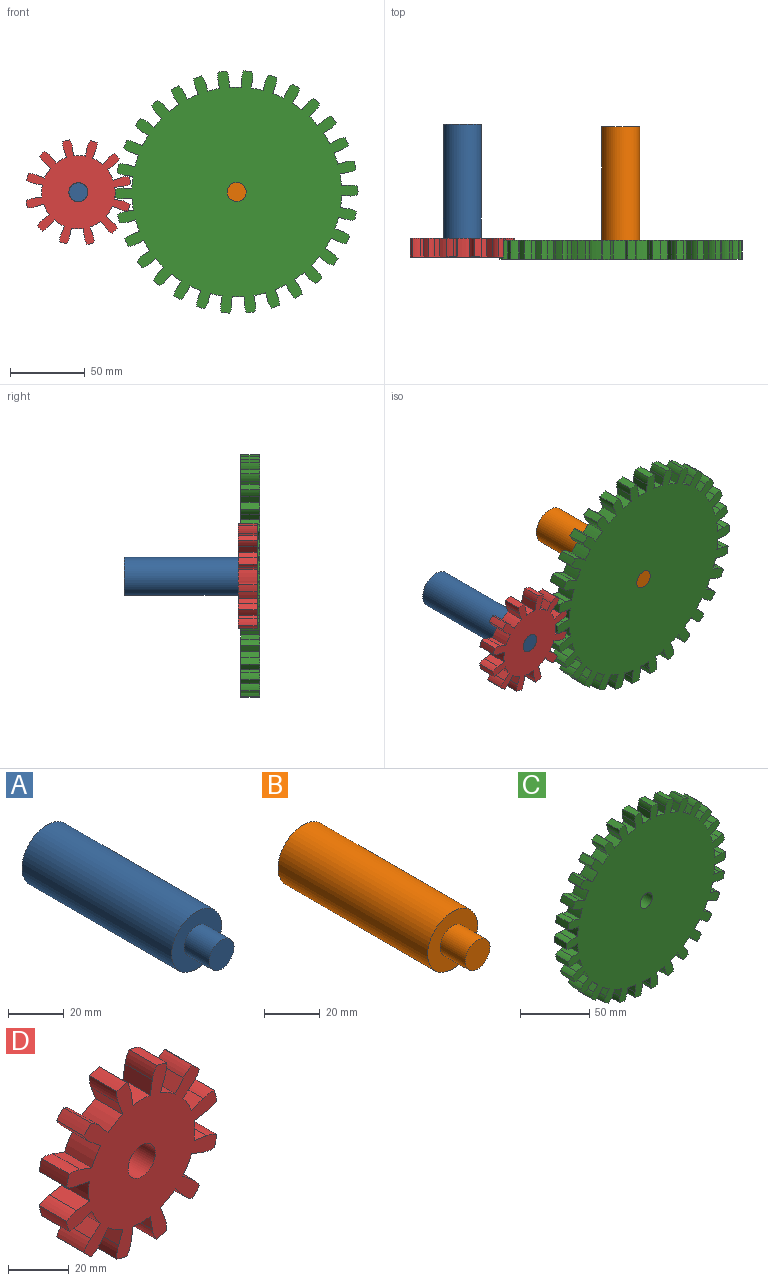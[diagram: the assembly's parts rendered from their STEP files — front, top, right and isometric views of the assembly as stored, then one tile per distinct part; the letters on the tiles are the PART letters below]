
ASSEMBLY  parts=4 mates=2
PART A: 5 faces, bbox 25.4x88.9x25.4 mm
  f0: plane 25.4x25.4mm, normal (0,-1,0), area 380mm2, adj f1,f3
  f1: cylinder r=12.7mm len=76.2mm, axis (0,-1,0), area 6080.5mm2, adj f0,f2
  f2: plane 25.4x25.4mm, normal (0,1,0), area 506.7mm2, adj f1
  f3: cylinder r=6.35mm len=12.7mm, axis (0,1,0), area 506.7mm2, adj f0,f4
  f4: plane 12.7x12.7mm, normal (0,-1,0), area 126.7mm2, adj f3
PART B: 5 faces, bbox 25.4x88.9x25.4 mm
  f0: plane 25.4x25.4mm, normal (0,-1,0), area 380mm2, adj f1,f3
  f1: cylinder r=12.7mm len=76.2mm, axis (0,-1,0), area 6080.5mm2, adj f0,f2
  f2: plane 25.4x25.4mm, normal (0,1,0), area 506.7mm2, adj f1
  f3: cylinder r=6.35mm len=12.7mm, axis (0,1,0), area 506.7mm2, adj f0,f4
  f4: plane 12.7x12.7mm, normal (0,-1,0), area 126.7mm2, adj f3
PART C: 183 faces, bbox 162.6x12.7x162.2 mm
  f0: plane 162.56x162.15mm, normal (0,-1,0), area 17686.6mm2, adj f2,f3,f4,f5,f6,f7,f8,f9
  f1: plane 162.56x162.15mm, normal (0,1,0), area 17686.6mm2, adj f2,f3,f4,f5,f6,f7,f8,f9
  f2: cylinder r=81.28mm len=12.7mm, axis (0,-1,0), area 70.3mm2, adj f0,f1,f177,f181
  f3: cylinder r=81.28mm len=12.7mm, axis (0,-1,0), area 70.3mm2, adj f0,f1,f172,f176
  f4: cylinder r=81.28mm len=12.7mm, axis (0,-1,0), area 70.3mm2, adj f0,f1,f167,f171
  f5: cylinder r=81.28mm len=12.7mm, axis (0,-1,0), area 70.3mm2, adj f0,f1,f162,f166
  f6: cylinder r=81.28mm len=12.7mm, axis (0,-1,0), area 70.3mm2, adj f0,f1,f157,f161
  f7: cylinder r=81.28mm len=12.7mm, axis (0,-1,0), area 70.3mm2, adj f0,f1,f152,f156
  f8: cylinder r=81.28mm len=12.7mm, axis (0,-1,0), area 70.3mm2, adj f0,f1,f147,f151
  f9: cylinder r=81.28mm len=12.7mm, axis (0,-1,0), area 70.3mm2, adj f0,f1,f142,f146
  f10: cylinder r=81.28mm len=12.7mm, axis (0,-1,0), area 70.3mm2, adj f0,f1,f137,f141
  f11: cylinder r=81.28mm len=12.7mm, axis (0,-1,0), area 70.3mm2, adj f0,f1,f132,f136
  f12: cylinder r=81.28mm len=12.7mm, axis (0,-1,0), area 70.3mm2, adj f0,f1,f127,f131
  f13: cylinder r=81.28mm len=12.7mm, axis (0,-1,0), area 70.3mm2, adj f0,f1,f122,f126
  f14: cylinder r=81.28mm len=12.7mm, axis (0,-1,0), area 70.3mm2, adj f0,f1,f117,f121
  f15: cylinder r=81.28mm len=12.7mm, axis (0,-1,0), area 70.3mm2, adj f0,f1,f112,f116
  f16: cylinder r=81.28mm len=12.7mm, axis (0,-1,0), area 70.3mm2, adj f0,f1,f107,f111
  f17: cylinder r=81.28mm len=12.7mm, axis (0,-1,0), area 70.3mm2, adj f0,f1,f102,f106
  f18: cylinder r=81.28mm len=12.7mm, axis (0,-1,0), area 70.3mm2, adj f0,f1,f97,f101
  f19: cylinder r=81.28mm len=12.7mm, axis (0,-1,0), area 70.3mm2, adj f0,f1,f92,f96
  f20: cylinder r=81.28mm len=12.7mm, axis (0,-1,0), area 70.3mm2, adj f0,f1,f87,f91
  f21: cylinder r=81.28mm len=12.7mm, axis (0,-1,0), area 70.3mm2, adj f0,f1,f82,f86
  f22: cylinder r=81.28mm len=12.7mm, axis (0,-1,0), area 70.3mm2, adj f0,f1,f77,f81
  f23: cylinder r=81.28mm len=12.7mm, axis (0,-1,0), area 70.3mm2, adj f0,f1,f72,f76
  f24: cylinder r=81.28mm len=12.7mm, axis (0,-1,0), area 70.3mm2, adj f0,f1,f67,f71
  f25: cylinder r=81.28mm len=12.7mm, axis (0,-1,0), area 70.3mm2, adj f0,f1,f62,f66
  f26: cylinder r=81.28mm len=12.7mm, axis (0,-1,0), area 70.3mm2, adj f0,f1,f57,f61
  f27: cylinder r=81.28mm len=12.7mm, axis (0,-1,0), area 70.3mm2, adj f0,f1,f52,f56
  f28: cylinder r=81.28mm len=12.7mm, axis (0,-1,0), area 70.3mm2, adj f0,f1,f47,f51
  f29: cylinder r=81.28mm len=12.7mm, axis (0,-1,0), area 70.3mm2, adj f0,f1,f41,f46
  f30: cylinder r=81.28mm len=12.7mm, axis (0,-1,0), area 70.3mm2, adj f0,f1,f36,f40
  f31: cylinder r=81.28mm len=12.7mm, axis (0,-1,0), area 70.3mm2, adj f0,f1,f35,f182
  f32: cylinder r=6.35mm len=12.7mm, axis (0,-1,0), area 506.7mm2, adj f0,f1
  f33: cylinder r=70.32mm len=12.7mm, axis (0,1,0), area 101.4mm2, adj f0,f1,f34,f37
  f34: plane 12.7x5.87mm, normal (-1,0,0.06), area 74.6mm2, adj f0,f1,f33,f35
  f35: cylinder r=11.96mm len=12.7mm, axis (0,1,0), area 66.5mm2, adj f0,f1,f31,f34
  f36: cylinder r=11.96mm len=12.7mm, axis (0,1,0), area 66.5mm2, adj f0,f1,f30,f37
  f37: plane 12.7x5.87mm, normal (1,0,0.06), area 74.6mm2, adj f0,f1,f33,f36
  f38: cylinder r=70.32mm len=12.7mm, axis (0,1,0), area 101.4mm2, adj f0,f1,f39,f42
  f39: plane 12.7x5.81mm, normal (-0.99,0,-0.15), area 74.6mm2, adj f0,f1,f38,f40
  f40: cylinder r=11.96mm len=12.7mm, axis (0,1,0), area 66.5mm2, adj f0,f1,f30,f39
  f41: cylinder r=11.96mm len=12.7mm, axis (0,1,0), area 66.5mm2, adj f0,f1,f29,f42
  f42: plane 12.7x5.67mm, normal (0.96,0,0.26), area 74.6mm2, adj f0,f1,f38,f41
  f43: cylinder r=70.32mm len=12.7mm, axis (0,1,0), area 101.4mm2, adj f0,f1,f44,f45
  f44: plane 12.7x5.5mm, normal (-0.94,0,-0.35), area 74.6mm2, adj f0,f1,f43,f46
  f45: plane 12.7x5.23mm, normal (0.89,0,0.46), area 74.6mm2, adj f0,f1,f43,f47
  f46: cylinder r=11.96mm len=12.7mm, axis (0,1,0), area 66.5mm2, adj f0,f1,f29,f44
  f47: cylinder r=11.96mm len=12.7mm, axis (0,1,0), area 66.5mm2, adj f0,f1,f28,f45
  f48: cylinder r=70.32mm len=12.7mm, axis (0,1,0), area 101.4mm2, adj f0,f1,f49,f50
  f49: plane 12.7x4.94mm, normal (-0.84,0,-0.54), area 74.6mm2, adj f0,f1,f48,f51
  f50: plane 12.7x4.55mm, normal (0.77,0,0.63), area 74.6mm2, adj f0,f1,f48,f52
  f51: cylinder r=11.96mm len=12.7mm, axis (0,1,0), area 66.5mm2, adj f0,f1,f28,f49
  f52: cylinder r=11.96mm len=12.7mm, axis (0,1,0), area 66.5mm2, adj f0,f1,f27,f50
  f53: cylinder r=70.32mm len=12.7mm, axis (0,1,0), area 101.4mm2, adj f0,f1,f54,f55
  f54: plane 12.7x4.17mm, normal (-0.71,0,-0.7), area 74.6mm2, adj f0,f1,f53,f56
  f55: plane 12.7x4.58mm, normal (0.63,0,0.78), area 74.6mm2, adj f0,f1,f53,f57
  f56: cylinder r=11.96mm len=12.7mm, axis (0,1,0), area 66.5mm2, adj f0,f1,f27,f54
  f57: cylinder r=11.96mm len=12.7mm, axis (0,1,0), area 66.5mm2, adj f0,f1,f26,f55
  f58: cylinder r=70.32mm len=12.7mm, axis (0,1,0), area 101.4mm2, adj f0,f1,f59,f60
  f59: plane 12.7x4.92mm, normal (-0.55,0,-0.84), area 74.6mm2, adj f0,f1,f58,f61
  f60: plane 12.7x5.25mm, normal (0.45,0,0.89), area 74.6mm2, adj f0,f1,f58,f62
  f61: cylinder r=11.96mm len=12.7mm, axis (0,1,0), area 66.5mm2, adj f0,f1,f26,f59
  f62: cylinder r=11.96mm len=12.7mm, axis (0,1,0), area 66.5mm2, adj f0,f1,f25,f60
  f63: cylinder r=70.32mm len=12.7mm, axis (0,1,0), area 101.4mm2, adj f0,f1,f64,f65
  f64: plane 12.7x5.48mm, normal (-0.36,0,-0.93), area 74.6mm2, adj f0,f1,f63,f66
  f65: plane 12.7x5.68mm, normal (0.25,0,0.97), area 74.6mm2, adj f0,f1,f63,f67
  f66: cylinder r=11.96mm len=12.7mm, axis (0,1,0), area 66.5mm2, adj f0,f1,f25,f64
  f67: cylinder r=11.96mm len=12.7mm, axis (0,1,0), area 66.5mm2, adj f0,f1,f24,f65
  f68: cylinder r=70.32mm len=12.7mm, axis (0,1,0), area 101.4mm2, adj f0,f1,f69,f70
  f69: plane 12.7x5.8mm, normal (-0.16,0,-0.99), area 74.6mm2, adj f0,f1,f68,f71
  f70: plane 12.7x5.87mm, normal (0.05,0,1), area 74.6mm2, adj f0,f1,f68,f72
  f71: cylinder r=11.96mm len=12.7mm, axis (0,1,0), area 66.5mm2, adj f0,f1,f24,f69
  f72: cylinder r=11.96mm len=12.7mm, axis (0,1,0), area 66.5mm2, adj f0,f1,f23,f70
  f73: cylinder r=70.32mm len=12.7mm, axis (0,1,0), area 101.4mm2, adj f0,f1,f74,f75
  f74: plane 12.7x5.87mm, normal (0.05,0,-1), area 74.6mm2, adj f0,f1,f73,f76
  f75: plane 12.7x5.8mm, normal (-0.16,0,0.99), area 74.6mm2, adj f0,f1,f73,f77
  f76: cylinder r=11.96mm len=12.7mm, axis (0,1,0), area 66.5mm2, adj f0,f1,f23,f74
  f77: cylinder r=11.96mm len=12.7mm, axis (0,1,0), area 66.5mm2, adj f0,f1,f22,f75
  f78: cylinder r=70.32mm len=12.7mm, axis (0,1,0), area 101.4mm2, adj f0,f1,f79,f80
  f79: plane 12.7x5.68mm, normal (0.25,0,-0.97), area 74.6mm2, adj f0,f1,f78,f81
  f80: plane 12.7x5.48mm, normal (-0.36,0,0.93), area 74.6mm2, adj f0,f1,f78,f82
  f81: cylinder r=11.96mm len=12.7mm, axis (0,1,0), area 66.5mm2, adj f0,f1,f22,f79
  f82: cylinder r=11.96mm len=12.7mm, axis (0,1,0), area 66.5mm2, adj f0,f1,f21,f80
  f83: cylinder r=70.32mm len=12.7mm, axis (0,1,0), area 101.4mm2, adj f0,f1,f84,f85
  f84: plane 12.7x5.25mm, normal (0.45,0,-0.89), area 74.6mm2, adj f0,f1,f83,f86
  f85: plane 12.7x4.92mm, normal (-0.55,0,0.84), area 74.6mm2, adj f0,f1,f83,f87
  f86: cylinder r=11.96mm len=12.7mm, axis (0,1,0), area 66.5mm2, adj f0,f1,f21,f84
  f87: cylinder r=11.96mm len=12.7mm, axis (0,1,0), area 66.5mm2, adj f0,f1,f20,f85
  f88: cylinder r=70.32mm len=12.7mm, axis (0,1,0), area 101.4mm2, adj f0,f1,f89,f90
  f89: plane 12.7x4.58mm, normal (0.63,0,-0.78), area 74.6mm2, adj f0,f1,f88,f91
  f90: plane 12.7x4.17mm, normal (-0.71,0,0.7), area 74.6mm2, adj f0,f1,f88,f92
  f91: cylinder r=11.96mm len=12.7mm, axis (0,1,0), area 66.5mm2, adj f0,f1,f20,f89
  f92: cylinder r=11.96mm len=12.7mm, axis (0,1,0), area 66.5mm2, adj f0,f1,f19,f90
  f93: cylinder r=70.32mm len=12.7mm, axis (0,1,0), area 101.4mm2, adj f0,f1,f94,f95
  f94: plane 12.7x4.55mm, normal (0.77,0,-0.63), area 74.6mm2, adj f0,f1,f93,f96
  f95: plane 12.7x4.94mm, normal (-0.84,0,0.54), area 74.6mm2, adj f0,f1,f93,f97
  f96: cylinder r=11.96mm len=12.7mm, axis (0,1,0), area 66.5mm2, adj f0,f1,f19,f94
  f97: cylinder r=11.96mm len=12.7mm, axis (0,1,0), area 66.5mm2, adj f0,f1,f18,f95
  f98: cylinder r=70.32mm len=12.7mm, axis (0,1,0), area 101.4mm2, adj f0,f1,f99,f100
  f99: plane 12.7x5.23mm, normal (0.89,0,-0.46), area 74.6mm2, adj f0,f1,f98,f101
  f100: plane 12.7x5.5mm, normal (-0.94,0,0.35), area 74.6mm2, adj f0,f1,f98,f102
  f101: cylinder r=11.96mm len=12.7mm, axis (0,1,0), area 66.5mm2, adj f0,f1,f18,f99
  f102: cylinder r=11.96mm len=12.7mm, axis (0,1,0), area 66.5mm2, adj f0,f1,f17,f100
  f103: cylinder r=70.32mm len=12.7mm, axis (0,1,0), area 101.4mm2, adj f0,f1,f104,f105
  f104: plane 12.7x5.67mm, normal (0.96,0,-0.26), area 74.6mm2, adj f0,f1,f103,f106
  f105: plane 12.7x5.81mm, normal (-0.99,0,0.15), area 74.6mm2, adj f0,f1,f103,f107
  f106: cylinder r=11.96mm len=12.7mm, axis (0,1,0), area 66.5mm2, adj f0,f1,f17,f104
  f107: cylinder r=11.96mm len=12.7mm, axis (0,1,0), area 66.5mm2, adj f0,f1,f16,f105
  f108: cylinder r=70.32mm len=12.7mm, axis (0,1,0), area 101.4mm2, adj f0,f1,f109,f110
  f109: plane 12.7x5.87mm, normal (1,0,-0.06), area 74.6mm2, adj f0,f1,f108,f111
  f110: plane 12.7x5.87mm, normal (-1,0,-0.06), area 74.6mm2, adj f0,f1,f108,f112
  f111: cylinder r=11.96mm len=12.7mm, axis (0,1,0), area 66.5mm2, adj f0,f1,f16,f109
  f112: cylinder r=11.96mm len=12.7mm, axis (0,1,0), area 66.5mm2, adj f0,f1,f15,f110
  f113: cylinder r=70.32mm len=12.7mm, axis (0,1,0), area 101.4mm2, adj f0,f1,f114,f115
  f114: plane 12.7x5.81mm, normal (0.99,0,0.15), area 74.6mm2, adj f0,f1,f113,f116
  f115: plane 12.7x5.67mm, normal (-0.96,0,-0.26), area 74.6mm2, adj f0,f1,f113,f117
  f116: cylinder r=11.96mm len=12.7mm, axis (0,1,0), area 66.5mm2, adj f0,f1,f15,f114
  f117: cylinder r=11.96mm len=12.7mm, axis (0,1,0), area 66.5mm2, adj f0,f1,f14,f115
  f118: cylinder r=70.32mm len=12.7mm, axis (0,1,0), area 101.4mm2, adj f0,f1,f119,f120
  f119: plane 12.7x5.5mm, normal (0.94,0,0.35), area 74.6mm2, adj f0,f1,f118,f121
  f120: plane 12.7x5.23mm, normal (-0.89,0,-0.46), area 74.6mm2, adj f0,f1,f118,f122
  f121: cylinder r=11.96mm len=12.7mm, axis (0,1,0), area 66.5mm2, adj f0,f1,f14,f119
  f122: cylinder r=11.96mm len=12.7mm, axis (0,1,0), area 66.5mm2, adj f0,f1,f13,f120
  f123: cylinder r=70.32mm len=12.7mm, axis (0,1,0), area 101.4mm2, adj f0,f1,f124,f125
  f124: plane 12.7x4.94mm, normal (0.84,0,0.54), area 74.6mm2, adj f0,f1,f123,f126
  f125: plane 12.7x4.55mm, normal (-0.77,0,-0.63), area 74.6mm2, adj f0,f1,f123,f127
  f126: cylinder r=11.96mm len=12.7mm, axis (0,1,0), area 66.5mm2, adj f0,f1,f13,f124
  f127: cylinder r=11.96mm len=12.7mm, axis (0,1,0), area 66.5mm2, adj f0,f1,f12,f125
  f128: cylinder r=70.32mm len=12.7mm, axis (0,1,0), area 101.4mm2, adj f0,f1,f129,f130
  f129: plane 12.7x4.17mm, normal (0.71,0,0.7), area 74.6mm2, adj f0,f1,f128,f131
  f130: plane 12.7x4.58mm, normal (-0.63,0,-0.78), area 74.6mm2, adj f0,f1,f128,f132
  f131: cylinder r=11.96mm len=12.7mm, axis (0,1,0), area 66.5mm2, adj f0,f1,f12,f129
  f132: cylinder r=11.96mm len=12.7mm, axis (0,1,0), area 66.5mm2, adj f0,f1,f11,f130
  f133: cylinder r=70.32mm len=12.7mm, axis (0,1,0), area 101.4mm2, adj f0,f1,f134,f135
  f134: plane 12.7x4.92mm, normal (0.55,0,0.84), area 74.6mm2, adj f0,f1,f133,f136
  f135: plane 12.7x5.25mm, normal (-0.45,0,-0.89), area 74.6mm2, adj f0,f1,f133,f137
  f136: cylinder r=11.96mm len=12.7mm, axis (0,1,0), area 66.5mm2, adj f0,f1,f11,f134
  f137: cylinder r=11.96mm len=12.7mm, axis (0,1,0), area 66.5mm2, adj f0,f1,f10,f135
  f138: cylinder r=70.32mm len=12.7mm, axis (0,1,0), area 101.4mm2, adj f0,f1,f139,f140
  f139: plane 12.7x5.48mm, normal (0.36,0,0.93), area 74.6mm2, adj f0,f1,f138,f141
  f140: plane 12.7x5.68mm, normal (-0.25,0,-0.97), area 74.6mm2, adj f0,f1,f138,f142
  f141: cylinder r=11.96mm len=12.7mm, axis (0,1,0), area 66.5mm2, adj f0,f1,f10,f139
  f142: cylinder r=11.96mm len=12.7mm, axis (0,1,0), area 66.5mm2, adj f0,f1,f9,f140
  f143: cylinder r=70.32mm len=12.7mm, axis (0,1,0), area 101.4mm2, adj f0,f1,f144,f145
  f144: plane 12.7x5.8mm, normal (0.16,0,0.99), area 74.6mm2, adj f0,f1,f143,f146
  f145: plane 12.7x5.87mm, normal (-0.05,0,-1), area 74.6mm2, adj f0,f1,f143,f147
  f146: cylinder r=11.96mm len=12.7mm, axis (0,1,0), area 66.5mm2, adj f0,f1,f9,f144
  f147: cylinder r=11.96mm len=12.7mm, axis (0,1,0), area 66.5mm2, adj f0,f1,f8,f145
  f148: cylinder r=70.32mm len=12.7mm, axis (0,1,0), area 101.4mm2, adj f0,f1,f149,f150
  f149: plane 12.7x5.87mm, normal (-0.05,0,1), area 74.6mm2, adj f0,f1,f148,f151
  f150: plane 12.7x5.8mm, normal (0.16,0,-0.99), area 74.6mm2, adj f0,f1,f148,f152
  f151: cylinder r=11.96mm len=12.7mm, axis (0,1,0), area 66.5mm2, adj f0,f1,f8,f149
  f152: cylinder r=11.96mm len=12.7mm, axis (0,1,0), area 66.5mm2, adj f0,f1,f7,f150
  f153: cylinder r=70.32mm len=12.7mm, axis (0,1,0), area 101.4mm2, adj f0,f1,f154,f155
  f154: plane 12.7x5.68mm, normal (-0.25,0,0.97), area 74.6mm2, adj f0,f1,f153,f156
  f155: plane 12.7x5.48mm, normal (0.36,0,-0.93), area 74.6mm2, adj f0,f1,f153,f157
  f156: cylinder r=11.96mm len=12.7mm, axis (0,1,0), area 66.5mm2, adj f0,f1,f7,f154
  f157: cylinder r=11.96mm len=12.7mm, axis (0,1,0), area 66.5mm2, adj f0,f1,f6,f155
  f158: cylinder r=70.32mm len=12.7mm, axis (0,1,0), area 101.4mm2, adj f0,f1,f159,f160
  f159: plane 12.7x5.25mm, normal (-0.45,0,0.89), area 74.6mm2, adj f0,f1,f158,f161
  f160: plane 12.7x4.92mm, normal (0.55,0,-0.84), area 74.6mm2, adj f0,f1,f158,f162
  f161: cylinder r=11.96mm len=12.7mm, axis (0,1,0), area 66.5mm2, adj f0,f1,f6,f159
  f162: cylinder r=11.96mm len=12.7mm, axis (0,1,0), area 66.5mm2, adj f0,f1,f5,f160
  f163: cylinder r=70.32mm len=12.7mm, axis (0,1,0), area 101.4mm2, adj f0,f1,f164,f165
  f164: plane 12.7x4.58mm, normal (-0.63,0,0.78), area 74.6mm2, adj f0,f1,f163,f166
  f165: plane 12.7x4.17mm, normal (0.71,0,-0.7), area 74.6mm2, adj f0,f1,f163,f167
  f166: cylinder r=11.96mm len=12.7mm, axis (0,1,0), area 66.5mm2, adj f0,f1,f5,f164
  f167: cylinder r=11.96mm len=12.7mm, axis (0,1,0), area 66.5mm2, adj f0,f1,f4,f165
  f168: cylinder r=70.32mm len=12.7mm, axis (0,1,0), area 101.4mm2, adj f0,f1,f169,f170
  f169: plane 12.7x4.55mm, normal (-0.77,0,0.63), area 74.6mm2, adj f0,f1,f168,f171
  f170: plane 12.7x4.94mm, normal (0.84,0,-0.54), area 74.6mm2, adj f0,f1,f168,f172
  f171: cylinder r=11.96mm len=12.7mm, axis (0,1,0), area 66.5mm2, adj f0,f1,f4,f169
  f172: cylinder r=11.96mm len=12.7mm, axis (0,1,0), area 66.5mm2, adj f0,f1,f3,f170
  f173: cylinder r=70.32mm len=12.7mm, axis (0,1,0), area 101.4mm2, adj f0,f1,f174,f175
  f174: plane 12.7x5.23mm, normal (-0.89,0,0.46), area 74.6mm2, adj f0,f1,f173,f176
  f175: plane 12.7x5.5mm, normal (0.94,0,-0.35), area 74.6mm2, adj f0,f1,f173,f177
  f176: cylinder r=11.96mm len=12.7mm, axis (0,1,0), area 66.5mm2, adj f0,f1,f3,f174
  f177: cylinder r=11.96mm len=12.7mm, axis (0,1,0), area 66.5mm2, adj f0,f1,f2,f175
  f178: cylinder r=70.32mm len=12.7mm, axis (0,1,0), area 101.4mm2, adj f0,f1,f179,f180
  f179: plane 12.7x5.67mm, normal (-0.96,0,0.26), area 74.6mm2, adj f0,f1,f178,f181
  f180: plane 12.7x5.81mm, normal (0.99,0,-0.15), area 74.6mm2, adj f0,f1,f178,f182
  f181: cylinder r=11.96mm len=12.7mm, axis (0,1,0), area 66.5mm2, adj f0,f1,f2,f179
  f182: cylinder r=11.96mm len=12.7mm, axis (0,1,0), area 66.5mm2, adj f0,f1,f31,f180
PART D: 75 faces, bbox 69.8x12.7x69.8 mm
  f0: plane 69.78x69.78mm, normal (0,-1,0), area 2517.7mm2, adj f2,f3,f4,f5,f6,f7,f8,f9
  f1: plane 69.78x69.78mm, normal (0,1,0), area 2517.7mm2, adj f2,f3,f4,f5,f6,f7,f8,f9
  f2: cylinder r=35.56mm len=12.7mm, axis (0,-1,0), area 61mm2, adj f0,f1,f69,f73
  f3: cylinder r=35.56mm len=12.7mm, axis (0,-1,0), area 61mm2, adj f0,f1,f64,f68
  f4: cylinder r=35.56mm len=12.7mm, axis (0,-1,0), area 61mm2, adj f0,f1,f59,f63
  f5: cylinder r=35.56mm len=12.7mm, axis (0,-1,0), area 61mm2, adj f0,f1,f54,f58
  f6: cylinder r=35.56mm len=12.7mm, axis (0,-1,0), area 61mm2, adj f0,f1,f49,f53
  f7: cylinder r=35.56mm len=12.7mm, axis (0,-1,0), area 61mm2, adj f0,f1,f44,f48
  f8: cylinder r=35.56mm len=12.7mm, axis (0,-1,0), area 61mm2, adj f0,f1,f39,f43
  f9: cylinder r=35.56mm len=12.7mm, axis (0,-1,0), area 61mm2, adj f0,f1,f34,f38
  f10: cylinder r=35.56mm len=12.7mm, axis (0,-1,0), area 61mm2, adj f0,f1,f29,f33
  f11: cylinder r=35.56mm len=12.7mm, axis (0,-1,0), area 61mm2, adj f0,f1,f24,f28
  f12: cylinder r=35.56mm len=12.7mm, axis (0,-1,0), area 61mm2, adj f0,f1,f19,f23
  f13: cylinder r=35.56mm len=12.7mm, axis (0,-1,0), area 61mm2, adj f0,f1,f18,f74
  f14: cylinder r=6.35mm len=12.7mm, axis (0,-1,0), area 506.7mm2, adj f0,f1
  f15: cylinder r=24.64mm len=12.7mm, axis (0,-1,0), area 101.8mm2, adj f0,f1,f16,f17
  f16: plane 12.7x5.77mm, normal (-0.99,0,0.16), area 74.2mm2, adj f0,f1,f15,f18
  f17: plane 12.7x5.77mm, normal (0.99,0,0.16), area 74.2mm2, adj f0,f1,f15,f19
  f18: cylinder r=11.96mm len=12.7mm, axis (0,-1,0), area 66.4mm2, adj f0,f1,f13,f16
  f19: cylinder r=11.96mm len=12.7mm, axis (0,-1,0), area 66.4mm2, adj f0,f1,f12,f17
  f20: cylinder r=24.64mm len=12.7mm, axis (0,-1,0), area 101.8mm2, adj f0,f1,f21,f22
  f21: plane 12.7x5.47mm, normal (-0.94,0,-0.35), area 74.2mm2, adj f0,f1,f20,f23
  f22: plane 12.7x4.52mm, normal (0.77,0,0.63), area 74.2mm2, adj f0,f1,f20,f24
  f23: cylinder r=11.96mm len=12.7mm, axis (0,-1,0), area 66.4mm2, adj f0,f1,f12,f21
  f24: cylinder r=11.96mm len=12.7mm, axis (0,-1,0), area 66.4mm2, adj f0,f1,f11,f22
  f25: cylinder r=24.64mm len=12.7mm, axis (0,-1,0), area 101.8mm2, adj f0,f1,f26,f27
  f26: plane 12.7x4.52mm, normal (-0.63,0,-0.77), area 74.2mm2, adj f0,f1,f25,f28
  f27: plane 12.7x5.47mm, normal (0.35,0,0.94), area 74.2mm2, adj f0,f1,f25,f29
  f28: cylinder r=11.96mm len=12.7mm, axis (0,-1,0), area 66.4mm2, adj f0,f1,f11,f26
  f29: cylinder r=11.96mm len=12.7mm, axis (0,-1,0), area 66.4mm2, adj f0,f1,f10,f27
  f30: cylinder r=24.64mm len=12.7mm, axis (0,-1,0), area 101.8mm2, adj f0,f1,f31,f32
  f31: plane 12.7x5.77mm, normal (-0.16,0,-0.99), area 74.2mm2, adj f0,f1,f30,f33
  f32: plane 12.7x5.77mm, normal (-0.16,0,0.99), area 74.2mm2, adj f0,f1,f30,f34
  f33: cylinder r=11.96mm len=12.7mm, axis (0,-1,0), area 66.4mm2, adj f0,f1,f10,f31
  f34: cylinder r=11.96mm len=12.7mm, axis (0,-1,0), area 66.4mm2, adj f0,f1,f9,f32
  f35: cylinder r=24.64mm len=12.7mm, axis (0,-1,0), area 101.8mm2, adj f0,f1,f36,f37
  f36: plane 12.7x5.47mm, normal (0.35,0,-0.94), area 74.2mm2, adj f0,f1,f35,f38
  f37: plane 12.7x4.52mm, normal (-0.63,0,0.77), area 74.2mm2, adj f0,f1,f35,f39
  f38: cylinder r=11.96mm len=12.7mm, axis (0,-1,0), area 66.4mm2, adj f0,f1,f9,f36
  f39: cylinder r=11.96mm len=12.7mm, axis (0,-1,0), area 66.4mm2, adj f0,f1,f8,f37
  f40: cylinder r=24.64mm len=12.7mm, axis (0,-1,0), area 101.8mm2, adj f0,f1,f41,f42
  f41: plane 12.7x4.52mm, normal (0.77,0,-0.63), area 74.2mm2, adj f0,f1,f40,f43
  f42: plane 12.7x5.47mm, normal (-0.94,0,0.35), area 74.2mm2, adj f0,f1,f40,f44
  f43: cylinder r=11.96mm len=12.7mm, axis (0,-1,0), area 66.4mm2, adj f0,f1,f8,f41
  f44: cylinder r=11.96mm len=12.7mm, axis (0,-1,0), area 66.4mm2, adj f0,f1,f7,f42
  f45: cylinder r=24.64mm len=12.7mm, axis (0,-1,0), area 101.8mm2, adj f0,f1,f46,f47
  f46: plane 12.7x5.77mm, normal (0.99,0,-0.16), area 74.2mm2, adj f0,f1,f45,f48
  f47: plane 12.7x5.77mm, normal (-0.99,0,-0.16), area 74.2mm2, adj f0,f1,f45,f49
  f48: cylinder r=11.96mm len=12.7mm, axis (0,-1,0), area 66.4mm2, adj f0,f1,f7,f46
  f49: cylinder r=11.96mm len=12.7mm, axis (0,-1,0), area 66.4mm2, adj f0,f1,f6,f47
  f50: cylinder r=24.64mm len=12.7mm, axis (0,-1,0), area 101.8mm2, adj f0,f1,f51,f52
  f51: plane 12.7x5.47mm, normal (0.94,0,0.35), area 74.2mm2, adj f0,f1,f50,f53
  f52: plane 12.7x4.52mm, normal (-0.77,0,-0.63), area 74.2mm2, adj f0,f1,f50,f54
  f53: cylinder r=11.96mm len=12.7mm, axis (0,-1,0), area 66.4mm2, adj f0,f1,f6,f51
  f54: cylinder r=11.96mm len=12.7mm, axis (0,-1,0), area 66.4mm2, adj f0,f1,f5,f52
  f55: cylinder r=24.64mm len=12.7mm, axis (0,-1,0), area 101.8mm2, adj f0,f1,f56,f57
  f56: plane 12.7x4.52mm, normal (0.63,0,0.77), area 74.2mm2, adj f0,f1,f55,f58
  f57: plane 12.7x5.47mm, normal (-0.35,0,-0.94), area 74.2mm2, adj f0,f1,f55,f59
  f58: cylinder r=11.96mm len=12.7mm, axis (0,-1,0), area 66.4mm2, adj f0,f1,f5,f56
  f59: cylinder r=11.96mm len=12.7mm, axis (0,-1,0), area 66.4mm2, adj f0,f1,f4,f57
  f60: cylinder r=24.64mm len=12.7mm, axis (0,-1,0), area 101.8mm2, adj f0,f1,f61,f62
  f61: plane 12.7x5.77mm, normal (0.16,0,0.99), area 74.2mm2, adj f0,f1,f60,f63
  f62: plane 12.7x5.77mm, normal (0.16,0,-0.99), area 74.2mm2, adj f0,f1,f60,f64
  f63: cylinder r=11.96mm len=12.7mm, axis (0,-1,0), area 66.4mm2, adj f0,f1,f4,f61
  f64: cylinder r=11.96mm len=12.7mm, axis (0,-1,0), area 66.4mm2, adj f0,f1,f3,f62
  f65: cylinder r=24.64mm len=12.7mm, axis (0,-1,0), area 101.8mm2, adj f0,f1,f66,f67
  f66: plane 12.7x5.47mm, normal (-0.35,0,0.94), area 74.2mm2, adj f0,f1,f65,f68
  f67: plane 12.7x4.52mm, normal (0.63,0,-0.77), area 74.2mm2, adj f0,f1,f65,f69
  f68: cylinder r=11.96mm len=12.7mm, axis (0,-1,0), area 66.4mm2, adj f0,f1,f3,f66
  f69: cylinder r=11.96mm len=12.7mm, axis (0,-1,0), area 66.4mm2, adj f0,f1,f2,f67
  f70: cylinder r=24.64mm len=12.7mm, axis (0,-1,0), area 101.8mm2, adj f0,f1,f71,f72
  f71: plane 12.7x4.52mm, normal (-0.77,0,0.63), area 74.2mm2, adj f0,f1,f70,f73
  f72: plane 12.7x5.47mm, normal (0.94,0,-0.35), area 74.2mm2, adj f0,f1,f70,f74
  f73: cylinder r=11.96mm len=12.7mm, axis (0,-1,0), area 66.4mm2, adj f0,f1,f2,f71
  f74: cylinder r=11.96mm len=12.7mm, axis (0,-1,0), area 66.4mm2, adj f0,f1,f13,f72
PLACE A t=(59.18,8.75,-25.54)mm fixed
PLACE B t=(165.28,7.18,0)mm fixed
PLACE C rot(axis=(0,-1,0),84.7deg) t=(98.39,0,-126.46)mm
PLACE D rot(axis=(0,1,0),31.8deg) t=(3.98,0.82,-0.14)mm
MATE revolute A.f1 <-> D.f2  axis (0,-1,0) through (3.98,-3.95,-0.14)mm
MATE revolute B.f1 <-> C.f2  axis (0,-1,0) through (110.08,-5.52,0)mm
